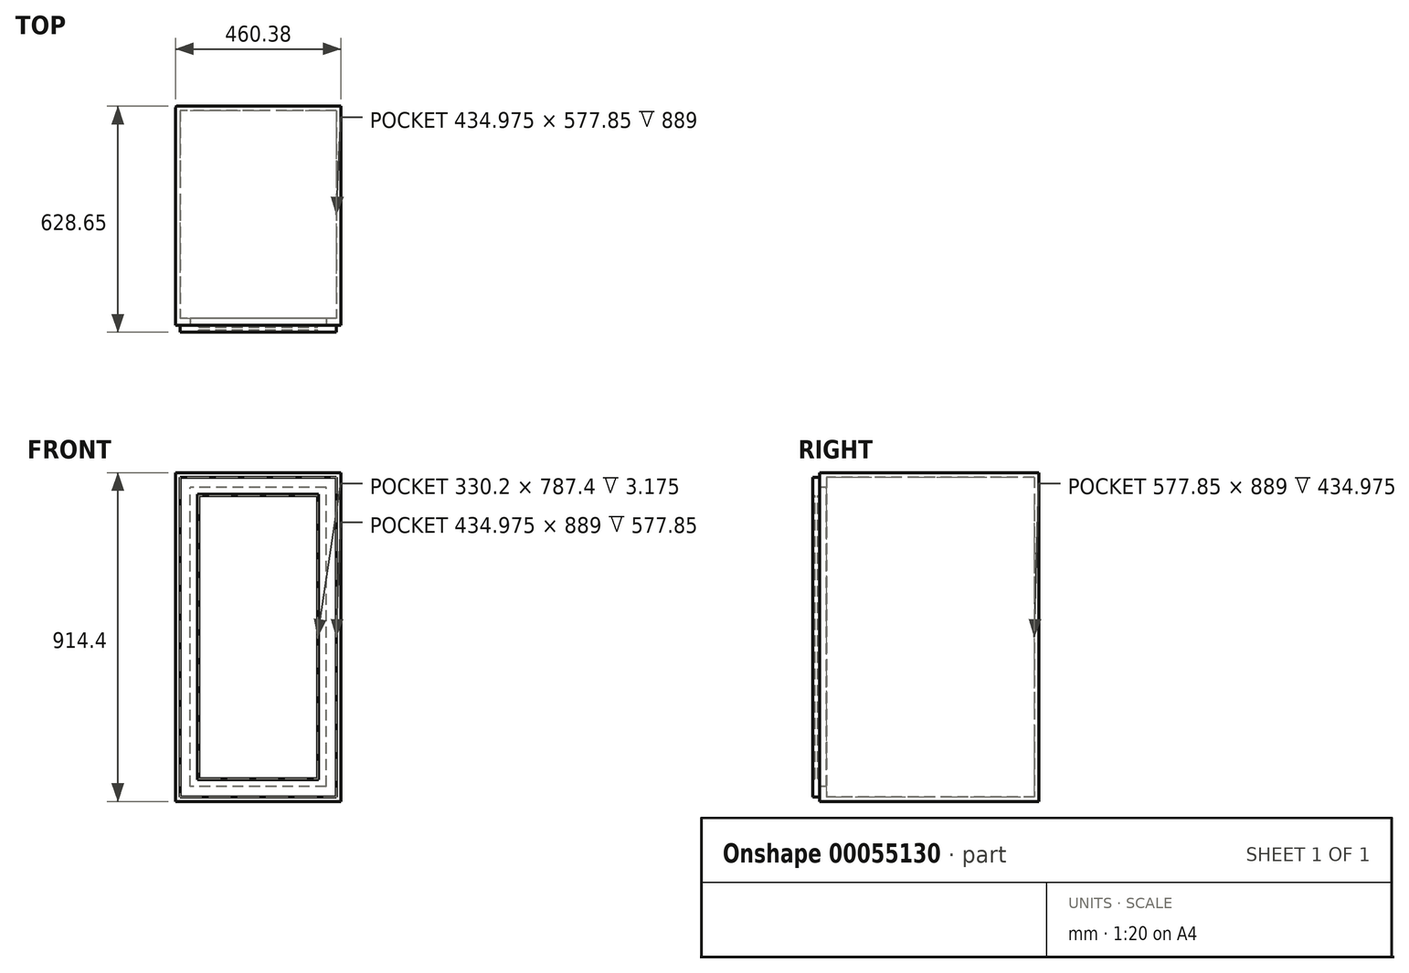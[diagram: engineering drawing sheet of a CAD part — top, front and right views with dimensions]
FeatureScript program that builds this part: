
annotation { "Feature Type Name" : "Feature", "Feature Type Description" : "" }
export const myFeature = defineFeature(function(context is Context, id is Id, definition is map)
    precondition{}
    {
        {
            var Q0;
            Q0=qCreatedBy(makeId("Top.planeOp"),FACE);
            var sketch = newSketch(context, id + "F0", { "sketchPlane" : qUnion([Q0])});
            skLineSegment(sketch, "E0.rect.bottom", {"start": v(230.19, 304.8) * mm, "end": v(-230.19, 304.8) * mm});
            skLineSegment(sketch, "E0.rect.top", {"start": v(230.19, -304.8) * mm, "end": v(-230.19, -304.8) * mm});
            skLineSegment(sketch, "E0.rect.left", {"start": v(230.19, 304.8) * mm, "end": v(230.19, -304.8) * mm});
            skLineSegment(sketch, "E0.rect.right", {"start": v(-230.19, 304.8) * mm, "end": v(-230.19, -304.8) * mm});
            skPoint(sketch, "E0.rect.middle", {"position": v(0, 0) * mm});
            skSolve(sketch);
        }
        {
            var Q0;
            Q0=qSketchRegion(id+"F0",true);
            extrude(context, id + "F1", {"entities" : qUnion([Q0]), "depth" : 914.4 * mm});
        }
        {
            var Q0;
            Q0=makeQuery(id+"F1.opExtrude","SWEPT_FACE",FACE,{"disambiguationData":[OSD([sQuery(id+"F0.wireOp",EDGE,"E0.rect.top")])]});
            shell(context, id + "F2", {"entities" : qUnion([Q0]), "thickness" : 12.7 * mm});
        }
        {
            var Q0;
            Q0=makeQuery(id+"F1.opExtrude","SWEPT_FACE",FACE,{"disambiguationData":[OSD([sQuery(id+"F0.wireOp",EDGE,"E0.rect.top")])]});
            var sketch = newSketch(context, id + "F3", { "sketchPlane" : qUnion([Q0])});
            skLineSegment(sketch, "E1", {"start": v(230.19, 914.4) * mm, "end": v(-230.19, 0) * mm, "construction": true});
            skLineSegment(sketch, "E2.rect.bottom", {"start": v(188.91, 41.28) * mm, "end": v(-188.91, 41.28) * mm});
            skLineSegment(sketch, "E2.rect.top", {"start": v(188.91, 873.12) * mm, "end": v(-188.91, 873.12) * mm});
            skLineSegment(sketch, "E2.rect.left", {"start": v(188.91, 41.28) * mm, "end": v(188.91, 873.13) * mm});
            skLineSegment(sketch, "E2.rect.right", {"start": v(-188.91, 41.28) * mm, "end": v(-188.91, 873.13) * mm});
            skPoint(sketch, "E2.rect.middle", {"position": v(0, 457.2) * mm});
            skLineSegment(sketch, "E3.rect.bottom", {"start": v(222.25, 6.35) * mm, "end": v(-222.25, 6.35) * mm});
            skLineSegment(sketch, "E3.rect.top", {"start": v(222.25, 908.05) * mm, "end": v(-222.25, 908.05) * mm});
            skLineSegment(sketch, "E3.rect.left", {"start": v(222.25, 6.35) * mm, "end": v(222.25, 908.05) * mm});
            skLineSegment(sketch, "E3.rect.right", {"start": v(-222.25, 6.35) * mm, "end": v(-222.25, 908.05) * mm});
            skLineSegment(sketch, "E4.rect.bottom", {"start": v(165.1, 63.5) * mm, "end": v(-165.1, 63.5) * mm});
            skLineSegment(sketch, "E4.rect.top", {"start": v(165.1, 850.9) * mm, "end": v(-165.1, 850.9) * mm});
            skLineSegment(sketch, "E4.rect.left", {"start": v(165.1, 63.5) * mm, "end": v(165.1, 850.9) * mm});
            skLineSegment(sketch, "E4.rect.right", {"start": v(-165.1, 63.5) * mm, "end": v(-165.1, 850.9) * mm});
            skSolve(sketch);
        }
        {
            var Q0;
            Q0=makeQuery(id+"F3.imprint","IMPRINT",FACE,{"disambiguationData":[TD([[makeQuery(id+"F3.imprint","IMPRINT",EDGE,{"derivedFrom":sQuery(id+"F3.wireOp",EDGE,"E2.rect.bottom")}),1.0]])]});
            var Q1;
            {var subQ0=sQuery(id+"F0.wireOp",EDGE,"E0.rect.top");var subQ3=makeQuery(id+"F1.opExtrude","CAP_EDGE",EDGE,{"disambiguationData":[OSD([subQ0])],"isStart":true});Q1=makeQuery(id+"F3.imprint","IMPRINT",FACE,{"disambiguationData":[TD([[makeQuery(id+"F3.imprint","IMPRINT",EDGE,{"derivedFrom":subQ3}),-1.0]])]});}
            extrude(context, id + "F4", {"entities" : qUnion([Q0, Q1]), "operationType" : NewBodyOperationType.ADD, "oppositeDirection" : true, "depth" : 19.05 * mm});
        }
        {
            var Q0;
            Q0=makeQuery(id+"F3.imprint","IMPRINT",FACE,{"disambiguationData":[TD([[makeQuery(id+"F3.imprint","IMPRINT",EDGE,{"derivedFrom":sQuery(id+"F3.wireOp",EDGE,"E2.rect.bottom")}),1.0]])]});
            var Q1;
            Q1=makeQuery(id+"F3.imprint","IMPRINT",FACE,{"disambiguationData":[TD([[makeQuery(id+"F3.imprint","IMPRINT",EDGE,{"derivedFrom":sQuery(id+"F3.wireOp",EDGE,"E2.rect.bottom")}),-1.0]])]});
            extrude(context, id + "F5", {"entities" : qUnion([Q0, Q1]), "operationType" : NewBodyOperationType.ADD, "depth" : 19.05 * mm});
        }
        {
            var Q0;
            Q0=makeQuery(id+"F5.opExtrude","SWEPT_FACE",FACE,{"disambiguationData":[OSD([sQuery(id+"F3.wireOp",EDGE,"E4.rect.top")])]});
            var sketch = newSketch(context, id + "F6", { "sketchPlane" : qUnion([Q0])});
            skLineSegment(sketch, "E5.bottom", {"start": v(-165.1, 309.56) * mm, "end": v(165.1, 309.56) * mm});
            skLineSegment(sketch, "E5.top", {"start": v(-165.1, 317.5) * mm, "end": v(165.1, 317.5) * mm});
            skLineSegment(sketch, "E5.left", {"start": v(-165.1, 309.56) * mm, "end": v(-165.1, 317.5) * mm});
            skLineSegment(sketch, "E5.right", {"start": v(165.1, 309.56) * mm, "end": v(165.1, 317.5) * mm});
            skSolve(sketch);
        }
        {
            var Q0;
            Q0=qSketchRegion(id+"F6",true);
            extrude(context, id + "F7", {"entities" : qUnion([Q0]), "operationType" : NewBodyOperationType.ADD, "endBound" : BoundingType.UP_TO_NEXT, "depth" : 25.4 * mm});
        }
        {
            var Q0;
            Q0=makeQuery(id+"F5.opExtrude","CAP_EDGE",EDGE,{"disambiguationData":[OSD([sQuery(id+"F3.wireOp",EDGE,"E4.rect.bottom")])],"isStart":false});
            var Q1;
            Q1=makeQuery(id+"F5.opExtrude","CAP_EDGE",EDGE,{"disambiguationData":[OSD([sQuery(id+"F3.wireOp",EDGE,"E4.rect.right")])],"isStart":false});
            var Q2;
            Q2=makeQuery(id+"F5.opExtrude","CAP_EDGE",EDGE,{"disambiguationData":[OSD([sQuery(id+"F3.wireOp",EDGE,"E4.rect.left")])],"isStart":false});
            var Q3;
            Q3=makeQuery(id+"F5.opExtrude","CAP_EDGE",EDGE,{"disambiguationData":[OSD([sQuery(id+"F3.wireOp",EDGE,"E4.rect.top")])],"isStart":false});
            var Q4;
            Q4=makeQuery(id+"F1.opExtrude","SWEPT_EDGE",EDGE,{"disambiguationData":[OSD([sQuery(id+"F0.wireOp",EDGE,"E0.rect.bottom"),sQuery(id+"F0.wireOp",EDGE,"E0.rect.right")])]});
            chamfer(context, id + "F8", {"entities" : qUnion([Q0, Q1, Q2, Q3, Q4]), "width" : 3.17 * mm, "tangentPropagation" : true});
        }
    });
